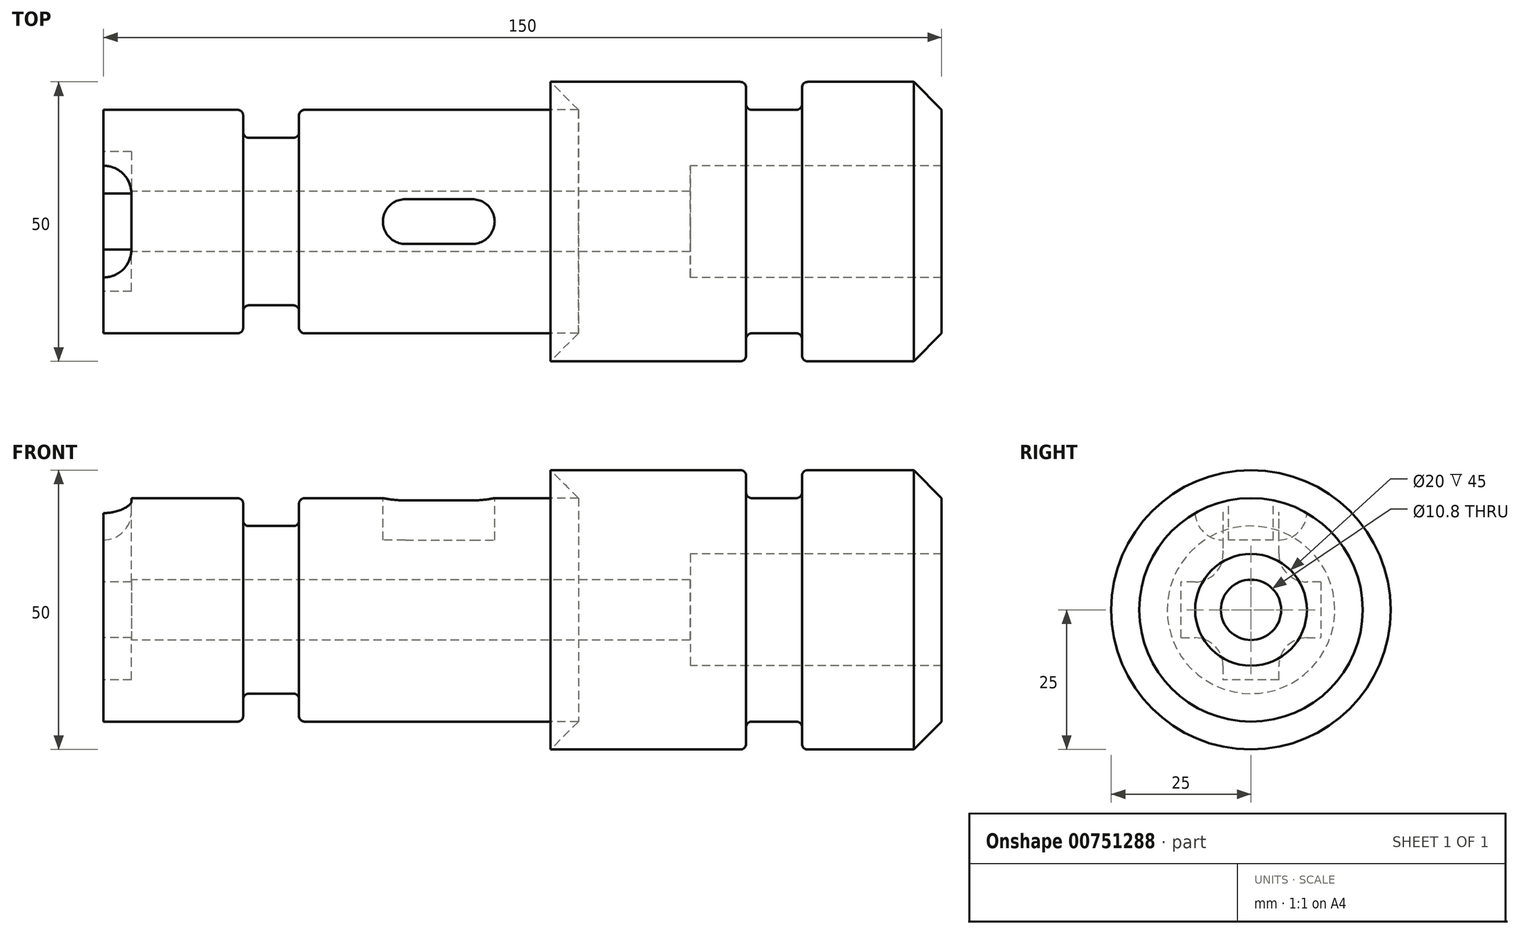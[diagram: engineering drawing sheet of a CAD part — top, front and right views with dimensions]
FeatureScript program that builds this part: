
annotation { "Feature Type Name" : "Feature", "Feature Type Description" : "" }
export const myFeature = defineFeature(function(context is Context, id is Id, definition is map)
    precondition{}
    {
        {
            var Q0;
            Q0=qCreatedBy(makeId("Front.planeOp"),FACE);
            var sketch = newSketch(context, id + "F0", { "sketchPlane" : qUnion([Q0])});
            skLineSegment(sketch, "E0", {"start": v(-75, 0) * mm, "end": v(-75, 20) * mm});
            skLineSegment(sketch, "E1", {"start": v(-75, 20) * mm, "end": v(-51, 20) * mm});
            skLineSegment(sketch, "E2", {"start": v(-50, 19) * mm, "end": v(-50, 16) * mm});
            skLineSegment(sketch, "E3", {"start": v(-49, 15) * mm, "end": v(-41, 15) * mm});
            skLineSegment(sketch, "E4", {"start": v(-40, 16) * mm, "end": v(-40, 19) * mm});
            skLineSegment(sketch, "E5", {"start": v(-39, 20) * mm, "end": v(10, 20) * mm});
            skLineSegment(sketch, "E6", {"start": v(10, 20) * mm, "end": v(5, 25) * mm});
            skLineSegment(sketch, "E7", {"start": v(5, 25) * mm, "end": v(39, 25) * mm});
            skLineSegment(sketch, "E8", {"start": v(40, 24) * mm, "end": v(40, 21) * mm});
            skLineSegment(sketch, "E9", {"start": v(41, 20) * mm, "end": v(49, 20) * mm});
            skLineSegment(sketch, "E10", {"start": v(50, 21) * mm, "end": v(50, 24) * mm});
            skLineSegment(sketch, "E11", {"start": v(51, 25) * mm, "end": v(75, 25) * mm});
            skLineSegment(sketch, "E12", {"start": v(75, 25) * mm, "end": v(75, 10) * mm});
            skLineSegment(sketch, "E13", {"start": v(75, 10) * mm, "end": v(30, 10) * mm});
            skLineSegment(sketch, "E14", {"start": v(30, 10) * mm, "end": v(30, 0) * mm});
            skLineSegment(sketch, "E15", {"start": v(30, 0) * mm, "end": v(-75, 0) * mm});
            skPoint(sketch, "E16.visualSharp", {"position": v(-50, 15) * mm});
            skArc(sketch, "E16.filletArc", {"start": v(-50, 16) * mm, "mid": v(-49.7, 15.3) * mm, "end": v(-49, 15) * mm});
            skPoint(sketch, "E17.visualSharp", {"position": v(-40, 15) * mm});
            skArc(sketch, "E17.filletArc", {"start": v(-41, 15) * mm, "mid": v(-40.3, 15.3) * mm, "end": v(-40, 16) * mm});
            skPoint(sketch, "E18.visualSharp", {"position": v(-40, 20) * mm});
            skArc(sketch, "E18.filletArc", {"start": v(-39, 20) * mm, "mid": v(-39.7, 19.7) * mm, "end": v(-40, 19) * mm});
            skPoint(sketch, "E19.visualSharp", {"position": v(-50, 20) * mm});
            skArc(sketch, "E19.filletArc", {"start": v(-50, 19) * mm, "mid": v(-50.3, 19.7) * mm, "end": v(-51, 20) * mm});
            skPoint(sketch, "E20.visualSharp", {"position": v(50, 20) * mm});
            skArc(sketch, "E20.filletArc", {"start": v(49, 20) * mm, "mid": v(49.7, 20.3) * mm, "end": v(50, 21) * mm});
            skPoint(sketch, "E21.visualSharp", {"position": v(50, 25) * mm});
            skArc(sketch, "E21.filletArc", {"start": v(51, 25) * mm, "mid": v(50.3, 24.7) * mm, "end": v(50, 24) * mm});
            skPoint(sketch, "E22.visualSharp", {"position": v(40, 25) * mm});
            skArc(sketch, "E22.filletArc", {"start": v(40, 24) * mm, "mid": v(39.7, 24.7) * mm, "end": v(39, 25) * mm});
            skPoint(sketch, "E23.visualSharp", {"position": v(40, 20) * mm});
            skArc(sketch, "E23.filletArc", {"start": v(40, 21) * mm, "mid": v(40.3, 20.3) * mm, "end": v(41, 20) * mm});
            skLineSegment(sketch, "E24", {"start": v(-125, 0) * mm, "end": v(125, 0) * mm});
            skSolve(sketch);
        }
        {
            var Q0;
            {var subQ1=sQuery(id+"F0.wireOp",EDGE,"E0");Q0=makeQuery(id+"F0.imprint","IMPRINT",FACE,{"disambiguationData":[TD([[makeQuery(id+"F0.imprint","IMPRINT",EDGE,{"derivedFrom":subQ1}),-1.0]])]});}
            var Q1;
            Q1=sQuery(id+"F0.wireOp",EDGE,"E24");
            revolve(context, id + "F1", {"surfaceOperationType" : NewSurfaceOperationType.NEW, "entities" : qUnion([Q0]), "axis" : qUnion([Q1]), "revolveType" : RevolveType.FULL});
        }
        {
            var Q0;
            Q0=qCreatedBy(makeId("Top.planeOp"),FACE);
            cPlane(context, id + "F2", {"entities" : qUnion([Q0]), "cplaneType" : CPlaneType.OFFSET, "offset" : 20 * mm, "width" : 150 * mm, "height" : 150 * mm});
        }
        {
            var Q0;
            Q0=qCreatedBy(id+"F2.planeOp",FACE);
            var sketch = newSketch(context, id + "F3", { "sketchPlane" : qUnion([Q0])});
            skLineSegment(sketch, "E25.bottom", {"start": v(-21, -4) * mm, "end": v(-9, -4) * mm});
            skLineSegment(sketch, "E25.top", {"start": v(-21, 4) * mm, "end": v(-9, 4) * mm});
            skLineSegment(sketch, "E25.left", {"start": v(-25, 0) * mm, "end": v(-25, 0) * mm});
            skLineSegment(sketch, "E25.right", {"start": v(-5, 0) * mm, "end": v(-5, 0) * mm});
            skPoint(sketch, "E26.visualSharp", {"position": v(-25, 4) * mm});
            skArc(sketch, "E26.filletArc", {"start": v(-21, 4) * mm, "mid": v(-23.83, 2.83) * mm, "end": v(-25, 0) * mm});
            skPoint(sketch, "E27.visualSharp", {"position": v(-25, -4) * mm});
            skArc(sketch, "E27.filletArc", {"start": v(-25, 0) * mm, "mid": v(-23.83, -2.83) * mm, "end": v(-21, -4) * mm});
            skPoint(sketch, "E28.visualSharp", {"position": v(-5, -4) * mm});
            skArc(sketch, "E28.filletArc", {"start": v(-9, -4) * mm, "mid": v(-6.17, -2.83) * mm, "end": v(-5, 0) * mm});
            skPoint(sketch, "E29.visualSharp", {"position": v(-5, 4) * mm});
            skArc(sketch, "E29.filletArc", {"start": v(-5, 0) * mm, "mid": v(-6.17, 2.83) * mm, "end": v(-9, 4) * mm});
            skLineSegment(sketch, "E30.bottom", {"start": v(-75, 10) * mm, "end": v(-75, 10) * mm});
            skLineSegment(sketch, "E30.top", {"start": v(-75, -10) * mm, "end": v(-75, -10) * mm});
            skLineSegment(sketch, "E30.left", {"start": v(-75, 10) * mm, "end": v(-75, -10) * mm});
            skLineSegment(sketch, "E30.right", {"start": v(-70, 5) * mm, "end": v(-70, -5) * mm});
            skLineSegment(sketch, "E31.0", {"start": v(-75, -20) * mm, "end": v(-75, 20) * mm});
            skPoint(sketch, "E32.visualSharp", {"position": v(-70, 10) * mm});
            skArc(sketch, "E32.filletArc", {"start": v(-70, 5) * mm, "mid": v(-71.46, 8.54) * mm, "end": v(-75, 10) * mm});
            skPoint(sketch, "E33.visualSharp", {"position": v(-70, -10) * mm});
            skArc(sketch, "E33.filletArc", {"start": v(-75, -10) * mm, "mid": v(-71.46, -8.54) * mm, "end": v(-70, -5) * mm});
            skSolve(sketch);
        }
        {
            var Q0;
            Q0 = qSketchRegion(id + "F3", true);
            extrude(context, id + "F4", {"entities" : qUnion([Q0]), "operationType" : NewBodyOperationType.REMOVE, "oppositeDirection" : true, "depth" : 7.5 * mm, "offsetDistance" : 25 * mm});
        }
        {
            var Q0;
            Q0=makeQuery(id+"F1.opRevolve","SWEPT_FACE",FACE,{"disambiguationData":[OSD([sQuery(id+"F0.wireOp",EDGE,"E0")])]});
            var sketch = newSketch(context, id + "F5", { "sketchPlane" : qUnion([Q0])});
            skLineSegment(sketch, "E34.0.0", {"start": v(-12.5, 10) * mm, "end": v(-12.5, -10) * mm, "construction": true});
            skLineSegment(sketch, "E34.0.1", {"start": v(-12.5, -10) * mm, "end": v(-17.32, -10) * mm, "construction": true});
            skArc(sketch, "E34.0.2", {"start": v(-17.32, -10) * mm, "mid": v(-14.14, -14.14) * mm, "end": v(-10, -17.32) * mm, "construction": true});
            skLineSegment(sketch, "E34.0.3", {"start": v(-10, -17.32) * mm, "end": v(-10, -12.5) * mm, "construction": true});
            skLineSegment(sketch, "E34.0.4", {"start": v(-10, -12.5) * mm, "end": v(10, -12.5) * mm, "construction": true});
            skLineSegment(sketch, "E34.0.5", {"start": v(10, -12.5) * mm, "end": v(10, -17.32) * mm, "construction": true});
            skArc(sketch, "E34.0.6", {"start": v(10, -17.32) * mm, "mid": v(14.14, -14.14) * mm, "end": v(17.32, -10) * mm, "construction": true});
            skLineSegment(sketch, "E34.0.7", {"start": v(17.32, -10) * mm, "end": v(12.5, -10) * mm, "construction": true});
            skLineSegment(sketch, "E34.0.8", {"start": v(12.5, -10) * mm, "end": v(12.5, 10) * mm, "construction": true});
            skLineSegment(sketch, "E34.0.9", {"start": v(12.5, 10) * mm, "end": v(17.32, 10) * mm, "construction": true});
            skArc(sketch, "E34.0.10", {"start": v(17.32, 10) * mm, "mid": v(14.14, 14.14) * mm, "end": v(10, 17.32) * mm, "construction": true});
            skLineSegment(sketch, "E34.0.11", {"start": v(10, 17.32) * mm, "end": v(10, 12.5) * mm, "construction": true});
            skLineSegment(sketch, "E34.0.12", {"start": v(10, 12.5) * mm, "end": v(-10, 12.5) * mm, "construction": true});
            skLineSegment(sketch, "E34.0.13", {"start": v(-10, 12.5) * mm, "end": v(-10, 17.32) * mm, "construction": true});
            skArc(sketch, "E34.0.14", {"start": v(-10, 17.32) * mm, "mid": v(-14.14, 14.14) * mm, "end": v(-17.32, 10) * mm, "construction": true});
            skLineSegment(sketch, "E34.0.15", {"start": v(-17.32, 10) * mm, "end": v(-12.5, 10) * mm, "construction": true});
            skLineSegment(sketch, "E35.0.0", {"start": v(-19.36, -5) * mm, "end": v(-12.5, -5) * mm, "construction": true});
            skLineSegment(sketch, "E35.0.1", {"start": v(-12.5, -5) * mm, "end": v(-12.5, 5) * mm, "construction": true});
            skLineSegment(sketch, "E35.0.2", {"start": v(-12.5, 5) * mm, "end": v(-19.36, 5) * mm, "construction": true});
            skArc(sketch, "E35.0.3", {"start": v(-19.36, -5) * mm, "mid": v(-20, 0) * mm, "end": v(-19.36, 5) * mm, "construction": true});
            skLineSegment(sketch, "E36.0.0", {"start": v(19.36, 5) * mm, "end": v(12.5, 5) * mm, "construction": true});
            skLineSegment(sketch, "E36.0.1", {"start": v(12.5, 5) * mm, "end": v(12.5, -5) * mm, "construction": true});
            skLineSegment(sketch, "E36.0.2", {"start": v(12.5, -5) * mm, "end": v(19.36, -5) * mm, "construction": true});
            skArc(sketch, "E36.0.3", {"start": v(19.36, 5) * mm, "mid": v(20, 0) * mm, "end": v(19.36, -5) * mm, "construction": true});
            skLineSegment(sketch, "E37.0.0", {"start": v(-5, 19.36) * mm, "end": v(-5, 12.5) * mm, "construction": true});
            skLineSegment(sketch, "E37.0.1", {"start": v(-5, 12.5) * mm, "end": v(5, 12.5) * mm, "construction": true});
            skLineSegment(sketch, "E37.0.2", {"start": v(5, 12.5) * mm, "end": v(5, 19.36) * mm, "construction": true});
            skArc(sketch, "E37.0.3", {"start": v(-5, 19.36) * mm, "mid": v(0, 20) * mm, "end": v(5, 19.36) * mm, "construction": true});
            skLineSegment(sketch, "E38.0.0", {"start": v(5, -19.36) * mm, "end": v(5, -12.5) * mm, "construction": true});
            skLineSegment(sketch, "E38.0.1", {"start": v(5, -12.5) * mm, "end": v(-5, -12.5) * mm, "construction": true});
            skLineSegment(sketch, "E38.0.2", {"start": v(-5, -12.5) * mm, "end": v(-5, -19.36) * mm, "construction": true});
            skArc(sketch, "E38.0.3", {"start": v(5, -19.36) * mm, "mid": v(0, -20) * mm, "end": v(-5, -19.36) * mm, "construction": true});
            skLineSegment(sketch, "E39", {"start": v(-12.5, 5) * mm, "end": v(-5, 5) * mm});
            skLineSegment(sketch, "E40", {"start": v(-5, 5) * mm, "end": v(-5, 12.5) * mm});
            skLineSegment(sketch, "E41", {"start": v(5, 12.5) * mm, "end": v(5, 5) * mm});
            skLineSegment(sketch, "E42", {"start": v(5, 5) * mm, "end": v(12.5, 5) * mm});
            skLineSegment(sketch, "E43", {"start": v(12.5, -5) * mm, "end": v(5, -5) * mm});
            skLineSegment(sketch, "E44", {"start": v(5, -5) * mm, "end": v(5, -12.5) * mm});
            skLineSegment(sketch, "E45", {"start": v(-5, -12.5) * mm, "end": v(-5, -5) * mm});
            skLineSegment(sketch, "E46", {"start": v(-5, -5) * mm, "end": v(-12.5, -5) * mm});
            skLineSegment(sketch, "E47", {"start": v(-12.5, 5) * mm, "end": v(-12.5, -5) * mm});
            skLineSegment(sketch, "E48", {"start": v(-5, -12.5) * mm, "end": v(5, -12.5) * mm});
            skLineSegment(sketch, "E49", {"start": v(12.5, -5) * mm, "end": v(12.5, 5) * mm});
            skLineSegment(sketch, "E50", {"start": v(5, 12.5) * mm, "end": v(-5, 12.5) * mm});
            skSolve(sketch);
        }
        {
            var Q0;
            Q0=makeQuery(id+"F5.imprint","IMPRINT",FACE,{"disambiguationData":[TD([[makeQuery(id+"F5.imprint","IMPRINT",EDGE,{"derivedFrom":sQuery(id+"F5.wireOp",EDGE,"E39")}),-1.0]])]});
            extrude(context, id + "F6", {"entities" : qUnion([Q0]), "operationType" : NewBodyOperationType.REMOVE, "oppositeDirection" : true, "depth" : 5 * mm, "offsetDistance" : 25 * mm});
        }
        {
            var Q0;
            Q0=makeQuery(id+"F4.boolean.opBoolean","COPY",EDGE,{"derivedFrom":makeQuery(id+"F4.opExtrude","CAP_EDGE",EDGE,{"disambiguationData":[OSD([sQuery(id+"F3.wireOp",EDGE,"E32.filletArc")])],"isStart":false})});
            var Q1;
            Q1=makeQuery(id+"F4.boolean.opBoolean","COPY",EDGE,{"derivedFrom":makeQuery(id+"F4.opExtrude","CAP_EDGE",EDGE,{"disambiguationData":[OSD([sQuery(id+"F3.wireOp",EDGE,"E33.filletArc")])],"isStart":false})});
            var Q2;
            Q2=makeQuery(id+"Fh4XnXklnlemPMK_1.1.F4.boolean.opBoolean","COPY",EDGE,{"derivedFrom":makeQuery(id+"Fh4XnXklnlemPMK_1.1.F4.opExtrude","CAP_EDGE",EDGE,{"disambiguationData":[OSD([sQuery(id+"F3.wireOp",EDGE,"E32.filletArc")])],"isStart":false})});
            var Q3;
            Q3=makeQuery(id+"Fh4XnXklnlemPMK_1.1.F4.boolean.opBoolean","COPY",EDGE,{"derivedFrom":makeQuery(id+"Fh4XnXklnlemPMK_1.1.F4.opExtrude","CAP_EDGE",EDGE,{"disambiguationData":[OSD([sQuery(id+"F3.wireOp",EDGE,"E33.filletArc")])],"isStart":false})});
            var Q4;
            Q4=makeQuery(id+"Fh4XnXklnlemPMK_1.3.F4.boolean.opBoolean","COPY",EDGE,{"derivedFrom":makeQuery(id+"Fh4XnXklnlemPMK_1.3.F4.opExtrude","CAP_EDGE",EDGE,{"disambiguationData":[OSD([sQuery(id+"F3.wireOp",EDGE,"E32.filletArc")])],"isStart":false})});
            var Q5;
            Q5=makeQuery(id+"Fh4XnXklnlemPMK_1.3.F4.boolean.opBoolean","COPY",EDGE,{"derivedFrom":makeQuery(id+"Fh4XnXklnlemPMK_1.3.F4.opExtrude","CAP_EDGE",EDGE,{"disambiguationData":[OSD([sQuery(id+"F3.wireOp",EDGE,"E33.filletArc")])],"isStart":false})});
            var Q6;
            Q6=makeQuery(id+"F6.boolean.opBoolean","COPY",EDGE,{"derivedFrom":makeQuery(id+"F6.opExtrude","SWEPT_EDGE",EDGE,{"disambiguationData":[OSD([sQuery(id+"F5.wireOp",EDGE,"E39"),sQuery(id+"F5.wireOp",EDGE,"E40")])]})});
            var Q7;
            Q7=makeQuery(id+"F6.boolean.opBoolean","COPY",EDGE,{"derivedFrom":makeQuery(id+"F6.opExtrude","SWEPT_EDGE",EDGE,{"disambiguationData":[OSD([sQuery(id+"F5.wireOp",EDGE,"E41"),sQuery(id+"F5.wireOp",EDGE,"E42")])]})});
            var Q8;
            Q8=makeQuery(id+"F6.boolean.opBoolean","COPY",EDGE,{"derivedFrom":makeQuery(id+"F6.opExtrude","SWEPT_EDGE",EDGE,{"disambiguationData":[OSD([sQuery(id+"F5.wireOp",EDGE,"E43"),sQuery(id+"F5.wireOp",EDGE,"E44")])]})});
            var Q9;
            Q9=makeQuery(id+"F6.boolean.opBoolean","COPY",EDGE,{"derivedFrom":makeQuery(id+"F6.opExtrude","SWEPT_EDGE",EDGE,{"disambiguationData":[OSD([sQuery(id+"F5.wireOp",EDGE,"E45"),sQuery(id+"F5.wireOp",EDGE,"E46")])]})});
            var Q10;
            Q10=makeQuery(id+"Fh4XnXklnlemPMK_1.2.F4.boolean.opBoolean","COPY",EDGE,{"derivedFrom":makeQuery(id+"Fh4XnXklnlemPMK_1.2.F4.opExtrude","CAP_EDGE",EDGE,{"disambiguationData":[OSD([sQuery(id+"F3.wireOp",EDGE,"E32.filletArc")])],"isStart":false})});
            var Q11;
            Q11=makeQuery(id+"Fh4XnXklnlemPMK_1.2.F4.boolean.opBoolean","COPY",EDGE,{"derivedFrom":makeQuery(id+"Fh4XnXklnlemPMK_1.2.F4.opExtrude","CAP_EDGE",EDGE,{"disambiguationData":[OSD([sQuery(id+"F3.wireOp",EDGE,"E33.filletArc")])],"isStart":false})});
            fillet(context, id + "F7", {"entities" : qUnion([Q0, Q1, Q2, Q3, Q4, Q5, Q6, Q7, Q8, Q9, Q10, Q11]), "radius" : 5 * mm, "tangentPropagation" : true, "allowEdgeOverflow" : false});
        }
        {
            var Q0;
            {var subQ0=sQuery(id+"F3.wireOp",EDGE,"E30.right");Q0=makeQuery(id+"F6.boolean.opBoolean","MERGE",FACE,{"derivedFrom":[makeQuery(id+"F4.boolean.opBoolean","COPY",FACE,{"derivedFrom":makeQuery(id+"F4.opExtrude","SWEPT_FACE",FACE,{"disambiguationData":[OSD([subQ0])]})}),makeQuery(id+"Fh4XnXklnlemPMK_1.1.F4.boolean.opBoolean","COPY",FACE,{"derivedFrom":makeQuery(id+"Fh4XnXklnlemPMK_1.1.F4.opExtrude","SWEPT_FACE",FACE,{"disambiguationData":[OSD([subQ0])]})}),makeQuery(id+"Fh4XnXklnlemPMK_1.2.F4.boolean.opBoolean","COPY",FACE,{"derivedFrom":makeQuery(id+"Fh4XnXklnlemPMK_1.2.F4.opExtrude","SWEPT_FACE",FACE,{"disambiguationData":[OSD([subQ0])]})}),makeQuery(id+"Fh4XnXklnlemPMK_1.3.F4.boolean.opBoolean","COPY",FACE,{"derivedFrom":makeQuery(id+"Fh4XnXklnlemPMK_1.3.F4.opExtrude","SWEPT_FACE",FACE,{"disambiguationData":[OSD([subQ0])]})}),makeQuery(id+"F6.opExtrude","CAP_FACE",FACE,{"disambiguationData":[OSD([sQuery(id+"F5.wireOp",EDGE,"E39"),sQuery(id+"F5.wireOp",EDGE,"E40"),sQuery(id+"F5.wireOp",EDGE,"E41"),sQuery(id+"F5.wireOp",EDGE,"E42"),sQuery(id+"F5.wireOp",EDGE,"E43"),sQuery(id+"F5.wireOp",EDGE,"E44"),sQuery(id+"F5.wireOp",EDGE,"E45"),sQuery(id+"F5.wireOp",EDGE,"E46"),sQuery(id+"F5.wireOp",EDGE,"E47"),sQuery(id+"F5.wireOp",EDGE,"E48"),sQuery(id+"F5.wireOp",EDGE,"E49"),sQuery(id+"F5.wireOp",EDGE,"E50")])],"isStart":false})]});}
            var sketch = newSketch(context, id + "F8", { "sketchPlane" : qUnion([Q0])});
            skLineSegment(sketch, "E51.0.0", {"start": v(-5, 19.36) * mm, "end": v(-5, 17.5) * mm});
            skLineSegment(sketch, "E51.0.1", {"start": v(-5, 17.5) * mm, "end": v(-5, 10) * mm});
            skArc(sketch, "E51.0.2", {"start": v(-5, 10) * mm, "mid": v(-6.46, 6.46) * mm, "end": v(-10, 5) * mm});
            skLineSegment(sketch, "E51.0.3", {"start": v(-10, 5) * mm, "end": v(-17.5, 5) * mm});
            skLineSegment(sketch, "E51.0.4", {"start": v(-17.5, 5) * mm, "end": v(-19.36, 5) * mm});
            skArc(sketch, "E51.0.5", {"start": v(-19.36, -5) * mm, "mid": v(-20, 0) * mm, "end": v(-19.36, 5) * mm});
            skLineSegment(sketch, "E51.0.6", {"start": v(-19.36, -5) * mm, "end": v(-17.5, -5) * mm});
            skLineSegment(sketch, "E51.0.7", {"start": v(-17.5, -5) * mm, "end": v(-10, -5) * mm});
            skArc(sketch, "E51.0.8", {"start": v(-10, -5) * mm, "mid": v(-6.46, -6.46) * mm, "end": v(-5, -10) * mm});
            skLineSegment(sketch, "E51.0.9", {"start": v(-5, -10) * mm, "end": v(-5, -17.5) * mm});
            skLineSegment(sketch, "E51.0.10", {"start": v(-5, -17.5) * mm, "end": v(-5, -19.36) * mm});
            skArc(sketch, "E51.0.11", {"start": v(5, -19.36) * mm, "mid": v(0, -20) * mm, "end": v(-5, -19.36) * mm});
            skLineSegment(sketch, "E51.0.12", {"start": v(5, -19.36) * mm, "end": v(5, -17.5) * mm});
            skLineSegment(sketch, "E51.0.13", {"start": v(5, -17.5) * mm, "end": v(5, -10) * mm});
            skArc(sketch, "E51.0.14", {"start": v(5, -10) * mm, "mid": v(6.46, -6.46) * mm, "end": v(10, -5) * mm});
            skLineSegment(sketch, "E51.0.15", {"start": v(10, -5) * mm, "end": v(17.5, -5) * mm});
            skLineSegment(sketch, "E51.0.16", {"start": v(17.5, -5) * mm, "end": v(19.36, -5) * mm});
            skArc(sketch, "E51.0.17", {"start": v(19.36, 5) * mm, "mid": v(20, 0) * mm, "end": v(19.36, -5) * mm});
            skLineSegment(sketch, "E51.0.18", {"start": v(19.36, 5) * mm, "end": v(17.5, 5) * mm});
            skLineSegment(sketch, "E51.0.19", {"start": v(17.5, 5) * mm, "end": v(10, 5) * mm});
            skArc(sketch, "E51.0.20", {"start": v(10, 5) * mm, "mid": v(6.46, 6.46) * mm, "end": v(5, 10) * mm});
            skLineSegment(sketch, "E51.0.21", {"start": v(5, 10) * mm, "end": v(5, 17.5) * mm});
            skLineSegment(sketch, "E51.0.22", {"start": v(5, 17.5) * mm, "end": v(5, 19.36) * mm});
            skArc(sketch, "E51.0.23", {"start": v(-5, 19.36) * mm, "mid": v(0, 20) * mm, "end": v(5, 19.36) * mm});
            skSolve(sketch);
        }
        {
            var Q0;
            Q0=sQuery(id+"F8.wireOp",VERTEX,"E51.0.5.center");
            var Q1;
            Q1=makeQuery(id+"F1.opRevolve","SWEPT_BODY",BODY,{"disambiguationData":[OSD([sQuery(id+"F0.wireOp",EDGE,"E0"),sQuery(id+"F0.wireOp",EDGE,"E1"),sQuery(id+"F0.wireOp",EDGE,"E2"),sQuery(id+"F0.wireOp",EDGE,"E3"),sQuery(id+"F0.wireOp",EDGE,"E4"),sQuery(id+"F0.wireOp",EDGE,"E5"),sQuery(id+"F0.wireOp",EDGE,"E6"),sQuery(id+"F0.wireOp",EDGE,"E7"),sQuery(id+"F0.wireOp",EDGE,"E8"),sQuery(id+"F0.wireOp",EDGE,"E9"),sQuery(id+"F0.wireOp",EDGE,"E10"),sQuery(id+"F0.wireOp",EDGE,"E11"),sQuery(id+"F0.wireOp",EDGE,"E12"),sQuery(id+"F0.wireOp",EDGE,"E13"),sQuery(id+"F0.wireOp",EDGE,"E14"),sQuery(id+"F0.wireOp",EDGE,"E16.filletArc"),sQuery(id+"F0.wireOp",EDGE,"E17.filletArc"),sQuery(id+"F0.wireOp",EDGE,"E18.filletArc"),sQuery(id+"F0.wireOp",EDGE,"E19.filletArc"),sQuery(id+"F0.wireOp",EDGE,"E20.filletArc"),sQuery(id+"F0.wireOp",EDGE,"E21.filletArc"),sQuery(id+"F0.wireOp",EDGE,"E22.filletArc"),sQuery(id+"F0.wireOp",EDGE,"E23.filletArc"),sQuery(id+"F0.wireOp",EDGE,"E24")])]});
            hole(context, id + "F9", {"style" : HoleStyle.SIMPLE, "endStyle" : HoleEndStyle.THROUGH, "standardTappedOrClearance" : lookupTablePath({ "standard" : "ISO", "engagement" : "75%", "pitch" : "1.25 mm", "size" : "M12", "type" : "Tapped" }), "standardBlindInLast" : lookupTablePath({ "standard" : "ISO", "engagement" : "75%", "pitch" : "1.25 mm", "size" : "M12", "type" : "Tapped" }), "holeDiameter" : 10.8 * mm, "majorDiameter" : 12 * mm, "showTappedDepth" : true, "isTappedThrough" : true, "tappedDepth" : 12 * mm, "tapClearance" : 3, "locations" : qUnion([Q0]), "scope" : qUnion([Q1])});
        }
        {
            var Q0;
            Q0=makeQuery(id+"F9.hole-0.boolean.opBoolean","INTERSECT",EDGE,{"derivedFrom":[makeQuery(id+"F1.opRevolve","SWEPT_FACE",FACE,{"disambiguationData":[OSD([sQuery(id+"F0.wireOp",EDGE,"E14")])]}),makeQuery(id+"F9.hole-0.opRevolve","SWEPT_FACE",FACE,{"disambiguationData":[OSD([sQuery(id+"F9.hole-0.sketch.wireOp",EDGE,"core_line_2")])]})]});
            var Q1;
            Q1=makeQuery(id+"F1.opRevolve","SWEPT_EDGE",EDGE,{"disambiguationData":[OSD([sQuery(id+"F0.wireOp",EDGE,"E11"),sQuery(id+"F0.wireOp",EDGE,"E12")])]});
            chamfer(context, id + "F10", {"entities" : qUnion([Q0, Q1]), "width" : 5 * mm, "tangentPropagation" : true});
        }
    });
